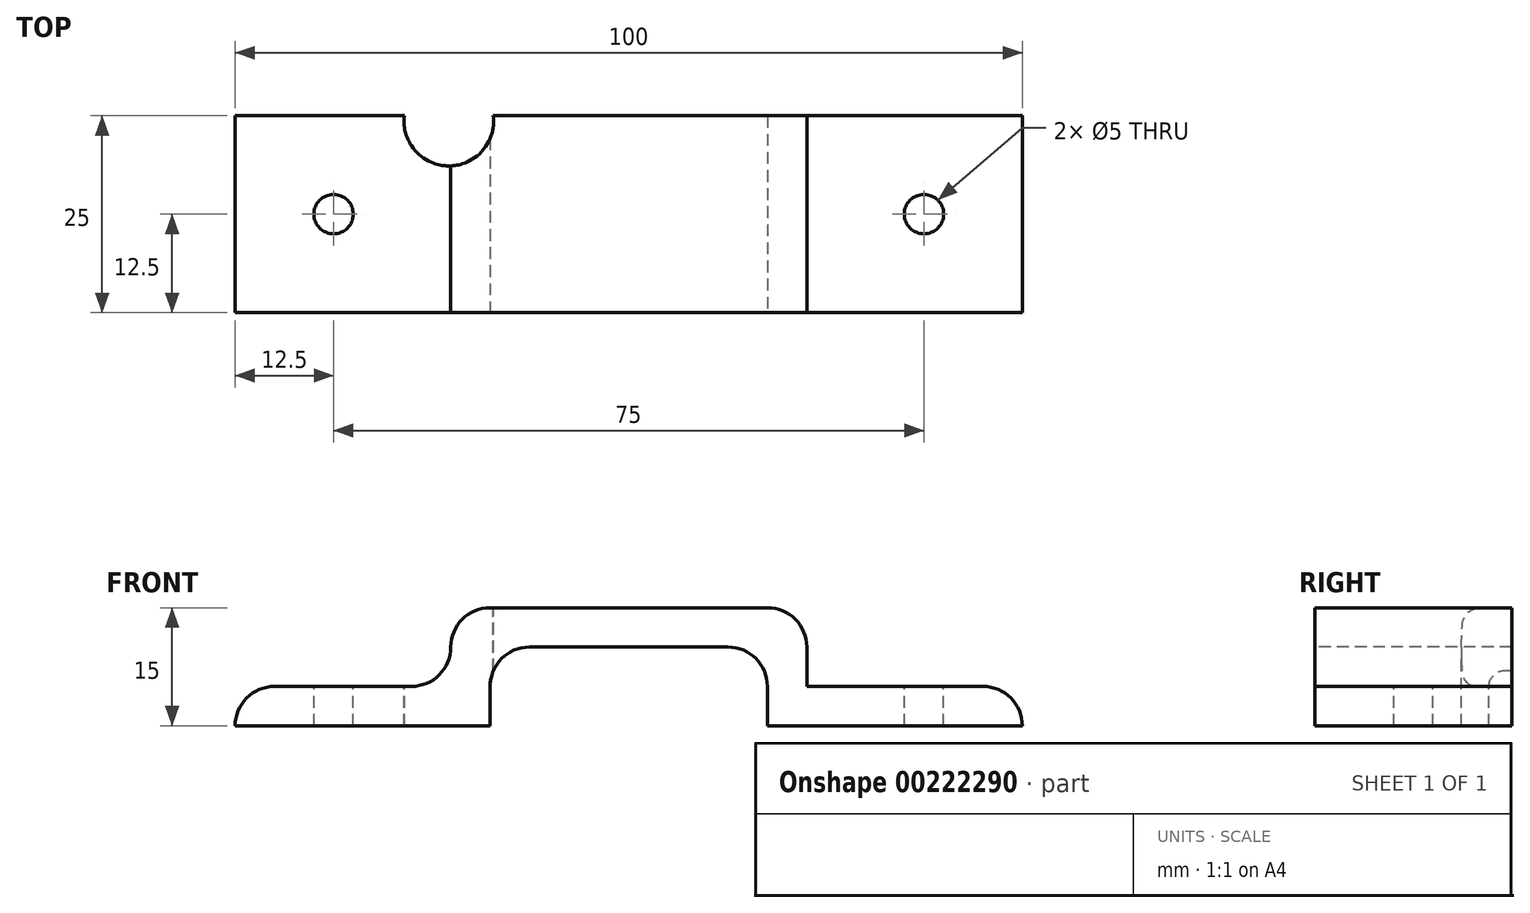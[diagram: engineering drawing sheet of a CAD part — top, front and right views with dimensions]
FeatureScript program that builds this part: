
annotation { "Feature Type Name" : "Feature", "Feature Type Description" : "" }
export const myFeature = defineFeature(function(context is Context, id is Id, definition is map)
    precondition{}
    {
        {
            var Q0;
            Q0=qCreatedBy(makeId("Top.planeOp"),FACE);
            var sketch = newSketch(context, id + "F0", { "sketchPlane" : qUnion([Q0])});
            skLineSegment(sketch, "E0.bottom", {"start": v(-50, -12.5) * mm, "end": v(50, -12.5) * mm});
            skLineSegment(sketch, "E0.top", {"start": v(-50, 12.5) * mm, "end": v(50, 12.5) * mm});
            skLineSegment(sketch, "E0.left", {"start": v(-50, -12.5) * mm, "end": v(-50, 12.5) * mm});
            skLineSegment(sketch, "E0.right", {"start": v(50, -12.5) * mm, "end": v(50, 12.5) * mm});
            skPoint(sketch, "E0.middle", {"position": v(0, 0) * mm});
            skSolve(sketch);
        }
        {
            var Q0;
            Q0 = qSketchRegion(id + "F0", true);
            extrude(context, id + "F1", {"entities" : qUnion([Q0]), "depth" : 5 * mm});
        }
        {
            var Q0;
            Q0=makeQuery(id+"F1.opExtrude","CAP_FACE",FACE,{"disambiguationData":[OSD([sQuery(id+"F0.wireOp",EDGE,"E0.bottom"),sQuery(id+"F0.wireOp",EDGE,"E0.top"),sQuery(id+"F0.wireOp",EDGE,"E0.left"),sQuery(id+"F0.wireOp",EDGE,"E0.right")])],"isStart":false});
            var sketch = newSketch(context, id + "F2", { "sketchPlane" : qUnion([Q0])});
            skCircle(sketch, "E1", {"center": v(-37.5, 0) * mm, "radius": 2.5 * mm});
            skCircle(sketch, "E2", {"center": v(37.5, 0) * mm, "radius": 2.5 * mm});
            skSolve(sketch);
        }
        {
            var Q0;
            Q0=makeQuery(id+"F2.imprint","IMPRINT",FACE,{"disambiguationData":[TD([[makeQuery(id+"F2.imprint","IMPRINT",EDGE,{"derivedFrom":sQuery(id+"F2.wireOp",EDGE,"E1")}),1.0]])]});
            var Q1;
            Q1=makeQuery(id+"F2.imprint","IMPRINT",FACE,{"disambiguationData":[TD([[makeQuery(id+"F2.imprint","IMPRINT",EDGE,{"derivedFrom":sQuery(id+"F2.wireOp",EDGE,"E2")}),1.0]])]});
            extrude(context, id + "F3", {"entities" : qUnion([Q0, Q1]), "operationType" : NewBodyOperationType.REMOVE, "oppositeDirection" : true, "depth" : 25 * mm});
        }
        {
            var Q0;
            Q0=makeQuery(id+"F1.opExtrude","CAP_FACE",FACE,{"disambiguationData":[OSD([sQuery(id+"F0.wireOp",EDGE,"E0.bottom"),sQuery(id+"F0.wireOp",EDGE,"E0.top"),sQuery(id+"F0.wireOp",EDGE,"E0.left"),sQuery(id+"F0.wireOp",EDGE,"E0.right")])],"isStart":false});
            var sketch = newSketch(context, id + "F4", { "sketchPlane" : qUnion([Q0])});
            skLineSegment(sketch, "E3.bottom", {"start": v(-22.62, -12.5) * mm, "end": v(22.62, -12.5) * mm});
            skLineSegment(sketch, "E3.top", {"start": v(-22.62, 12.5) * mm, "end": v(22.62, 12.5) * mm});
            skLineSegment(sketch, "E3.left", {"start": v(-22.62, -12.5) * mm, "end": v(-22.62, 12.5) * mm});
            skLineSegment(sketch, "E3.right", {"start": v(22.62, -12.5) * mm, "end": v(22.62, 12.5) * mm});
            skPoint(sketch, "E3.middle", {"position": v(0, 0) * mm});
            skSolve(sketch);
        }
        {
            var Q0;
            Q0 = qSketchRegion(id + "F4", true);
            extrude(context, id + "F5", {"entities" : qUnion([Q0]), "operationType" : NewBodyOperationType.ADD, "depth" : 10 * mm});
        }
        {
            var Q0;
            Q0=makeQuery(id+"F5.boolean.opBoolean","MERGE",FACE,{"derivedFrom":[makeQuery(id+"F1.opExtrude","SWEPT_FACE",FACE,{"disambiguationData":[OSD([sQuery(id+"F0.wireOp",EDGE,"E0.bottom")])]}),makeQuery(id+"F5.opExtrude","SWEPT_FACE",FACE,{"disambiguationData":[OSD([sQuery(id+"F4.wireOp",EDGE,"E3.bottom")])]})]});
            var sketch = newSketch(context, id + "F6", { "sketchPlane" : qUnion([Q0])});
            skLineSegment(sketch, "E4.bottom", {"start": v(-17.62, 10) * mm, "end": v(17.62, 10) * mm});
            skLineSegment(sketch, "E4.top", {"start": v(-17.62, -10) * mm, "end": v(17.62, -10) * mm});
            skLineSegment(sketch, "E4.left", {"start": v(-17.62, 10) * mm, "end": v(-17.62, -10) * mm});
            skLineSegment(sketch, "E4.right", {"start": v(17.62, 10) * mm, "end": v(17.62, -10) * mm});
            skPoint(sketch, "E4.middle", {"position": v(0, 0) * mm});
            skPoint(sketch, "E4.cornerSnap0", {"position": v(-22.62, 10) * mm});
            skSolve(sketch);
        }
        {
            var Q0;
            Q0 = qSketchRegion(id + "F6", true);
            extrude(context, id + "F7", {"entities" : qUnion([Q0]), "operationType" : NewBodyOperationType.REMOVE, "oppositeDirection" : true, "depth" : 78 * mm});
        }
        {
            var Q0;
            Q0=makeQuery(id+"F5.opExtrude","CAP_EDGE",EDGE,{"disambiguationData":[OSD([sQuery(id+"F4.wireOp",EDGE,"E3.right")])],"isStart":true});
            var Q1;
            Q1=makeQuery(id+"F5.opExtrude","CAP_EDGE",EDGE,{"disambiguationData":[OSD([sQuery(id+"F4.wireOp",EDGE,"E3.left")])],"isStart":true});
            var Q2;
            Q2=makeQuery(id+"F5.opExtrude","CAP_EDGE",EDGE,{"disambiguationData":[OSD([sQuery(id+"F4.wireOp",EDGE,"E3.left")])],"isStart":false});
            var Q3;
            Q3=makeQuery(id+"F5.opExtrude","CAP_EDGE",EDGE,{"disambiguationData":[OSD([sQuery(id+"F4.wireOp",EDGE,"E3.right")])],"isStart":false});
            var Q4;
            Q4=makeQuery(id+"F1.opExtrude","CAP_EDGE",EDGE,{"disambiguationData":[OSD([sQuery(id+"F0.wireOp",EDGE,"E0.right")])],"isStart":false});
            var Q5;
            Q5=makeQuery(id+"F1.opExtrude","CAP_EDGE",EDGE,{"disambiguationData":[OSD([sQuery(id+"F0.wireOp",EDGE,"E0.left")])],"isStart":false});
            var Q6;
            Q6=makeQuery(id+"F7.boolean.opBoolean","COPY",EDGE,{"derivedFrom":makeQuery(id+"F7.opExtrude","SWEPT_EDGE",EDGE,{"disambiguationData":[OSD([sQuery(id+"F6.wireOp",EDGE,"E4.bottom"),sQuery(id+"F6.wireOp",EDGE,"E4.left")])]})});
            var Q7;
            Q7=makeQuery(id+"F7.boolean.opBoolean","COPY",EDGE,{"derivedFrom":makeQuery(id+"F7.opExtrude","SWEPT_EDGE",EDGE,{"disambiguationData":[OSD([sQuery(id+"F6.wireOp",EDGE,"E4.bottom"),sQuery(id+"F6.wireOp",EDGE,"E4.right")])]})});
            fillet(context, id + "F8", {"entities" : qUnion([Q0, Q1, Q2, Q3, Q4, Q5, Q6, Q7]), "radius" : 5 * mm, "tangentPropagation" : true, "allowEdgeOverflow" : false});
        }
        {
            var Q0;
            {var subQ0=sQuery(id+"F0.wireOp",EDGE,"E0.right");var subQ1=sQuery(id+"F0.wireOp",EDGE,"E0.top");var subQ2=sQuery(id+"F0.wireOp",EDGE,"E0.bottom");Q0=makeQuery(id+"F5.boolean.opBoolean","SPLIT",FACE,{"disambiguationData":[TD([makeQuery(id+"F1.opExtrude","SWEPT_FACE",FACE,{"disambiguationData":[OSD([subQ0])]})])],"derivedFrom":makeQuery(id+"F1.opExtrude","CAP_FACE",FACE,{"disambiguationData":[OSD([subQ2,subQ1,sQuery(id+"F0.wireOp",EDGE,"E0.left"),subQ0])],"isStart":false})});}
            var sketch = newSketch(context, id + "F9", { "sketchPlane" : qUnion([Q0])});
            skCircle(sketch, "E5", {"center": v(-22.86, 11.8) * mm, "radius": 5.69 * mm});
            skSolve(sketch);
        }
        {
            var Q0;
            Q0 = qSketchRegion(id + "F9", true);
            extrude(context, id + "F10", {"entities" : qUnion([Q0]), "operationType" : NewBodyOperationType.REMOVE, "endBound" : BoundingType.SYMMETRIC, "oppositeDirection" : true, "depth" : 25 * mm});
        }
    });
